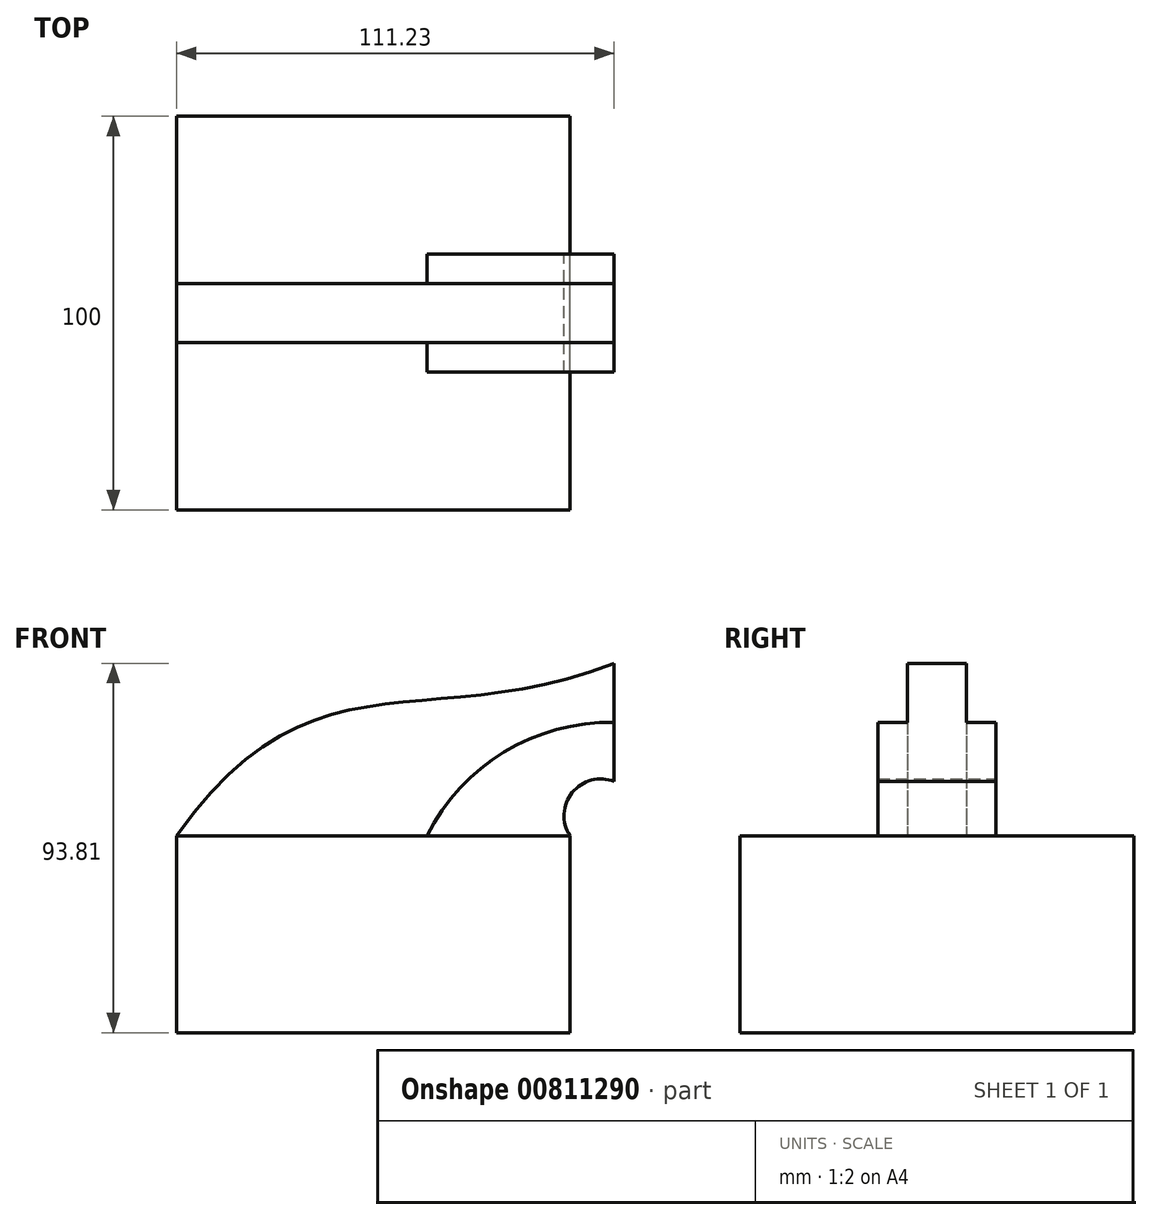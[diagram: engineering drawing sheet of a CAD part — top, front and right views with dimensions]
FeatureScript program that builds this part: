
annotation { "Feature Type Name" : "Feature", "Feature Type Description" : "" }
export const myFeature = defineFeature(function(context is Context, id is Id, definition is map)
    precondition{}
    {
        {
            var Q0;
            Q0=qCreatedBy(makeId("Front.planeOp"),FACE);
            var sketch = newSketch(context, id + "F0", { "sketchPlane" : qUnion([Q0])});
            skLineSegment(sketch, "E0.bottom", {"start": v(-45.86, 17.96) * mm, "end": v(54.14, 17.96) * mm});
            skLineSegment(sketch, "E0.top", {"start": v(-45.86, -32.04) * mm, "end": v(54.14, -32.04) * mm});
            skLineSegment(sketch, "E0.left", {"start": v(-45.86, 17.96) * mm, "end": v(-45.86, -32.04) * mm});
            skLineSegment(sketch, "E0.right", {"start": v(54.14, 17.96) * mm, "end": v(54.14, -32.04) * mm});
            skLineSegment(sketch, "E1.bottom", {"start": v(65.37, 61.77) * mm, "end": v(95.37, 61.77) * mm});
            skLineSegment(sketch, "E1.top", {"start": v(65.37, 31.77) * mm, "end": v(95.37, 31.77) * mm});
            skLineSegment(sketch, "E1.left", {"start": v(65.37, 61.77) * mm, "end": v(65.37, 31.77) * mm});
            skLineSegment(sketch, "E1.right", {"start": v(95.37, 61.77) * mm, "end": v(95.37, 31.77) * mm});
            skFitSpline(sketch, "E2", {"points": [v(65.37, 61.77) * mm, v(-45.86, 17.96) * mm], "startDerivative": vector(-142.68, -55.33) * mm, "endDerivative": vector(-103.2, -145.41) * mm});
            skArc(sketch, "E3", {"start": v(65.37, 46.77) * mm, "mid": v(37.4, 39.28) * mm, "end": v(17.8, 17.96) * mm});
            skArc(sketch, "E4", {"start": v(65.37, 31.77) * mm, "mid": v(54.7, 28.98) * mm, "end": v(54.14, 17.96) * mm});
            skLineSegment(sketch, "E5", {"start": v(80.37, 61.77) * mm, "end": v(80.37, 31.77) * mm});
            skSolve(sketch);
        }
        {
            var Q0;
            Q0=makeQuery(id+"F0.imprint","IMPRINT",FACE,{"disambiguationData":[TD([[makeQuery(id+"F0.imprint","IMPRINT",EDGE,{"derivedFrom":sQuery(id+"F0.wireOp",EDGE,"E0.top")}),1.0]])]});
            extrude(context, id + "F1", {"entities" : qUnion([Q0]), "endBound" : BoundingType.SYMMETRIC, "depth" : 100 * mm, "offsetDistance" : 25 * mm});
        }
        {
            var Q0;
            {var subQ2=sQuery(id+"F0.wireOp",EDGE,"E3");Q0=makeQuery(id+"F0.imprint","IMPRINT",FACE,{"disambiguationData":[TD([[makeQuery(id+"F0.imprint","IMPRINT",EDGE,{"derivedFrom":subQ2}),1.0]])]});}
            extrude(context, id + "F2", {"entities" : qUnion([Q0]), "operationType" : NewBodyOperationType.ADD, "endBound" : BoundingType.SYMMETRIC, "depth" : 30 * mm, "offsetDistance" : 25 * mm});
        }
        {
            var Q0;
            {var subQ0=sQuery(id+"F0.wireOp",EDGE,"E2");Q0=makeQuery(id+"F0.imprint","IMPRINT",FACE,{"disambiguationData":[TD([[makeQuery(id+"F0.imprint","IMPRINT",EDGE,{"derivedFrom":subQ0}),1.0]])]});}
            extrude(context, id + "F3", {"entities" : qUnion([Q0]), "operationType" : NewBodyOperationType.ADD, "endBound" : BoundingType.SYMMETRIC, "depth" : 15 * mm, "offsetDistance" : 25 * mm});
        }
    });
